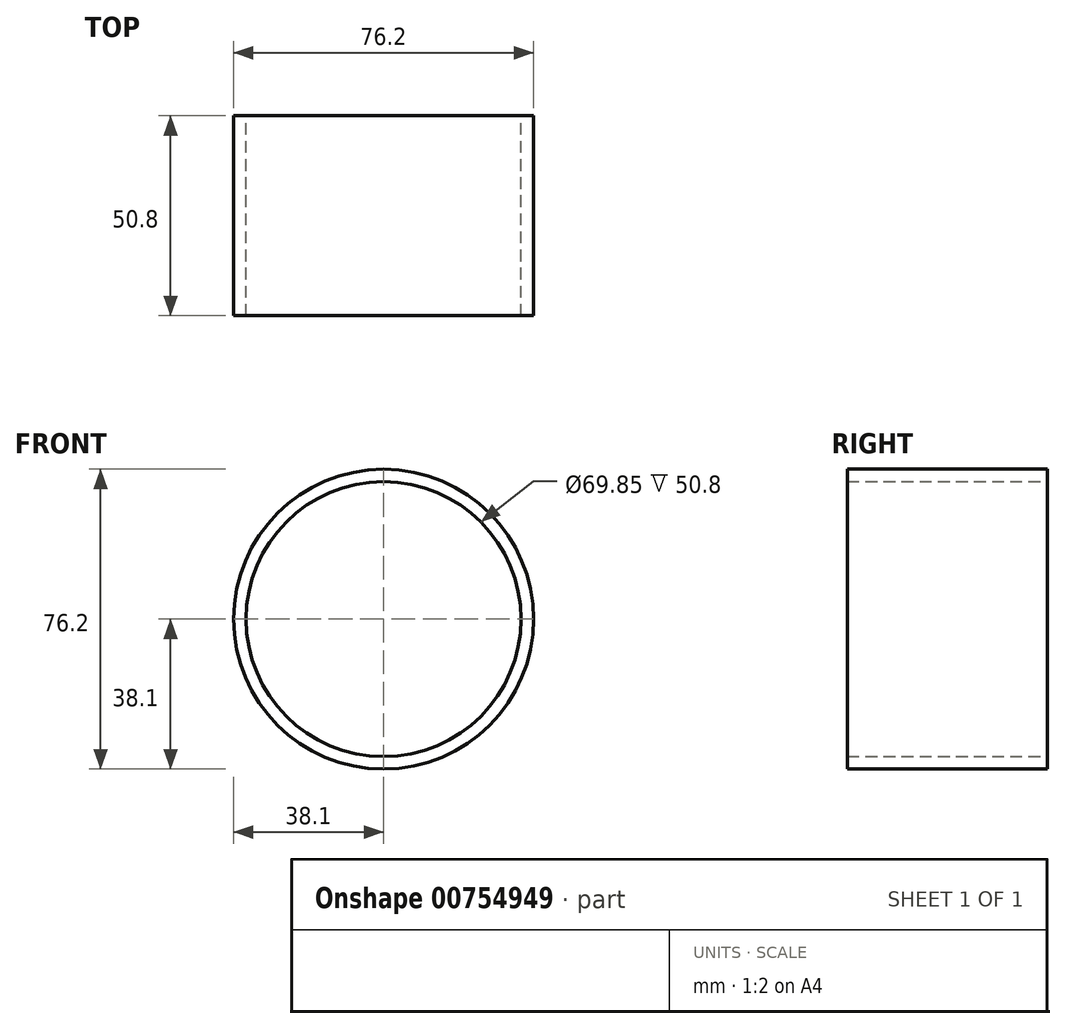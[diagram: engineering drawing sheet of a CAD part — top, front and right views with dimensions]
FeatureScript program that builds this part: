
annotation { "Feature Type Name" : "Feature", "Feature Type Description" : "" }
export const myFeature = defineFeature(function(context is Context, id is Id, definition is map)
    precondition{}
    {
        {
            var Q0;
            Q0=qCreatedBy(makeId("Front.planeOp"),FACE);
            var sketch = newSketch(context, id + "F0", { "sketchPlane" : qUnion([Q0])});
            skCircle(sketch, "E0", {"center": v(0, 0) * mm, "radius": 38.1 * mm});
            skCircle(sketch, "E1", {"center": v(0, 0) * mm, "radius": 34.93 * mm});
            skSolve(sketch);
        }
        {
            var Q0;
            Q0 = qSketchRegion(id + "F0", true);
            extrude(context, id + "F1", {"entities" : qUnion([Q0]), "depth" : 50.8 * mm, "offsetDistance" : 25.4 * mm});
        }
    });
